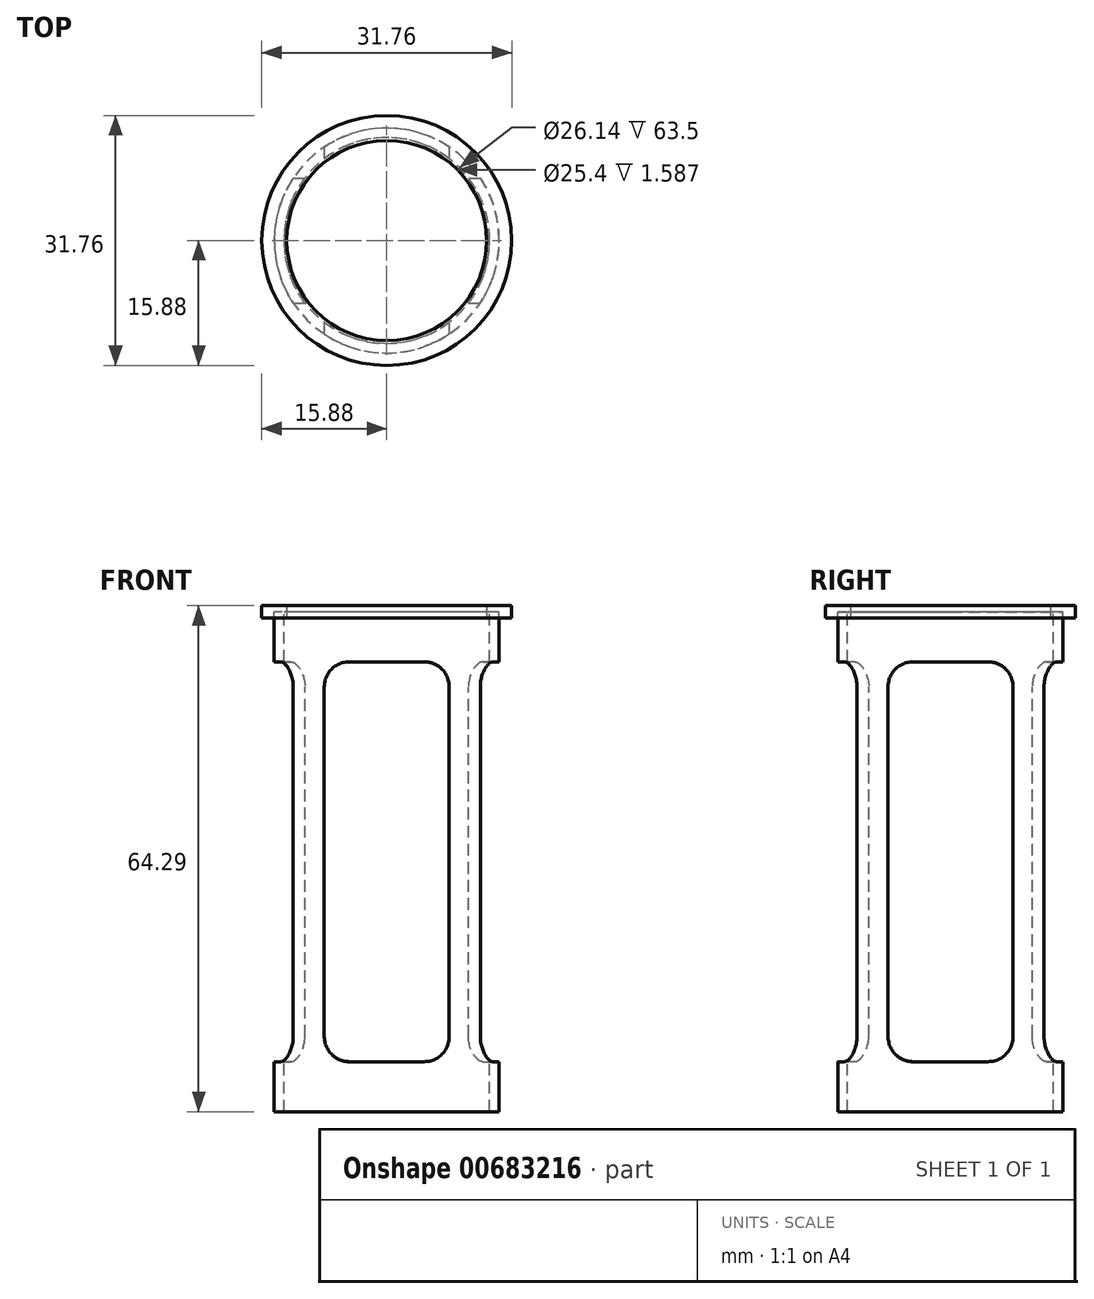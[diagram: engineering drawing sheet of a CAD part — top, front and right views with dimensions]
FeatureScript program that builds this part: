
annotation { "Feature Type Name" : "Feature", "Feature Type Description" : "" }
export const myFeature = defineFeature(function(context is Context, id is Id, definition is map)
    precondition{}
    {
        {
            var Q0;
            Q0=qCreatedBy(makeId("Top.planeOp"),FACE);
            var sketch = newSketch(context, id + "F0", { "sketchPlane" : qUnion([Q0])});
            skCircle(sketch, "E0", {"center": v(0, 0) * mm, "radius": 12.7 * mm});
            skCircle(sketch, "E1", {"center": v(0, 0) * mm, "radius": 15.88 * mm});
            skCircle(sketch, "E2", {"center": v(0, 0) * mm, "radius": 14.29 * mm});
            skCircle(sketch, "E3", {"center": v(0, 0) * mm, "radius": 13.07 * mm});
            skSolve(sketch);
        }
        {
            var Q0;
            Q0=makeQuery(id+"F0.imprint","IMPRINT",FACE,{"disambiguationData":[TD([[makeQuery(id+"F0.imprint","IMPRINT",EDGE,{"derivedFrom":sQuery(id+"F0.wireOp",EDGE,"E0")}),-1.0]])]});
            var Q1;
            Q1=makeQuery(id+"F0.imprint","IMPRINT",FACE,{"disambiguationData":[TD([[makeQuery(id+"F0.imprint","IMPRINT",EDGE,{"derivedFrom":sQuery(id+"F0.wireOp",EDGE,"E1")}),1.0]])]});
            var Q2;
            Q2=makeQuery(id+"F0.imprint","IMPRINT",FACE,{"disambiguationData":[TD([[makeQuery(id+"F0.imprint","IMPRINT",EDGE,{"derivedFrom":sQuery(id+"F0.wireOp",EDGE,"E2")}),1.0]])]});
            extrude(context, id + "F1", {"entities" : qUnion([Q0, Q1, Q2]), "endBound" : BoundingType.SYMMETRIC, "depth" : 1.59 * mm, "offsetDistance" : 25.4 * mm});
        }
        {
            var Q0;
            Q0=makeQuery(id+"F0.imprint","IMPRINT",FACE,{"disambiguationData":[TD([[makeQuery(id+"F0.imprint","IMPRINT",EDGE,{"derivedFrom":sQuery(id+"F0.wireOp",EDGE,"E2")}),1.0]])]});
            extrude(context, id + "F2", {"entities" : qUnion([Q0]), "oppositeDirection" : true, "depth" : 63.5 * mm, "offsetDistance" : 25.4 * mm});
        }
        {
            var Q0;
            Q0=qCreatedBy(makeId("Right.planeOp"),FACE);
            var sketch = newSketch(context, id + "F3", { "sketchPlane" : qUnion([Q0])});
            skLineSegment(sketch, "E4.bottom", {"start": v(-4.76, -6.35) * mm, "end": v(4.76, -6.35) * mm});
            skLineSegment(sketch, "E4.top", {"start": v(-4.76, -57.15) * mm, "end": v(4.76, -57.15) * mm});
            skLineSegment(sketch, "E4.left", {"start": v(-7.94, -9.53) * mm, "end": v(-7.94, -53.98) * mm});
            skLineSegment(sketch, "E4.right", {"start": v(7.94, -9.53) * mm, "end": v(7.94, -53.98) * mm});
            skPoint(sketch, "E5.visualSharp", {"position": v(-7.94, -6.35) * mm});
            skArc(sketch, "E5.filletArc", {"start": v(-4.76, -6.35) * mm, "mid": v(-7, -7.28) * mm, "end": v(-7.94, -9.53) * mm});
            skPoint(sketch, "E6.visualSharp", {"position": v(7.94, -6.35) * mm});
            skArc(sketch, "E6.filletArc", {"start": v(7.94, -9.53) * mm, "mid": v(7, -7.28) * mm, "end": v(4.76, -6.35) * mm});
            skPoint(sketch, "E7.visualSharp", {"position": v(7.94, -57.15) * mm});
            skArc(sketch, "E7.filletArc", {"start": v(4.76, -57.15) * mm, "mid": v(7, -56.22) * mm, "end": v(7.94, -53.98) * mm});
            skPoint(sketch, "E8.visualSharp", {"position": v(-7.94, -57.15) * mm});
            skArc(sketch, "E8.filletArc", {"start": v(-7.94, -53.98) * mm, "mid": v(-7, -56.22) * mm, "end": v(-4.76, -57.15) * mm});
            skSolve(sketch);
        }
        {
            var Q0;
            Q0=makeQuery(id+"F3.imprint","IMPRINT",FACE,{"disambiguationData":[TD([[makeQuery(id+"F3.imprint","IMPRINT",EDGE,{"derivedFrom":sQuery(id+"F3.wireOp",EDGE,"E4.bottom")}),-1.0]])]});
            extrude(context, id + "F4", {"entities" : qUnion([Q0]), "operationType" : NewBodyOperationType.REMOVE, "endBound" : BoundingType.SYMMETRIC, "oppositeDirection" : true, "depth" : 31.75 * mm, "offsetDistance" : 25.4 * mm});
        }
        {
            var Q0;
            Q0=qCreatedBy(makeId("Front.planeOp"),FACE);
            var sketch = newSketch(context, id + "F5", { "sketchPlane" : qUnion([Q0])});
            skLineSegment(sketch, "E9.bottom", {"start": v(4.76, -6.35) * mm, "end": v(-4.76, -6.35) * mm});
            skLineSegment(sketch, "E9.top", {"start": v(4.76, -57.15) * mm, "end": v(-4.76, -57.15) * mm});
            skLineSegment(sketch, "E9.left", {"start": v(7.94, -9.52) * mm, "end": v(7.94, -53.98) * mm});
            skLineSegment(sketch, "E9.right", {"start": v(-7.94, -9.53) * mm, "end": v(-7.94, -53.98) * mm});
            skPoint(sketch, "E10.visualSharp", {"position": v(7.94, -6.35) * mm});
            skArc(sketch, "E10.filletArc", {"start": v(7.94, -9.52) * mm, "mid": v(7, -7.28) * mm, "end": v(4.76, -6.35) * mm});
            skPoint(sketch, "E11.visualSharp", {"position": v(-7.94, -6.35) * mm});
            skArc(sketch, "E11.filletArc", {"start": v(-4.76, -6.35) * mm, "mid": v(-7, -7.28) * mm, "end": v(-7.94, -9.53) * mm});
            skPoint(sketch, "E12.visualSharp", {"position": v(-7.94, -57.15) * mm});
            skArc(sketch, "E12.filletArc", {"start": v(-7.94, -53.98) * mm, "mid": v(-7, -56.22) * mm, "end": v(-4.76, -57.15) * mm});
            skPoint(sketch, "E13.visualSharp", {"position": v(7.94, -57.15) * mm});
            skArc(sketch, "E13.filletArc", {"start": v(4.76, -57.15) * mm, "mid": v(7, -56.22) * mm, "end": v(7.94, -53.98) * mm});
            skSolve(sketch);
        }
        {
            var Q0;
            Q0 = qSketchRegion(id + "F5", true);
            extrude(context, id + "F6", {"entities" : qUnion([Q0]), "operationType" : NewBodyOperationType.REMOVE, "endBound" : BoundingType.SYMMETRIC, "oppositeDirection" : true, "depth" : 31.75 * mm, "offsetDistance" : 25.4 * mm});
        }
    });
